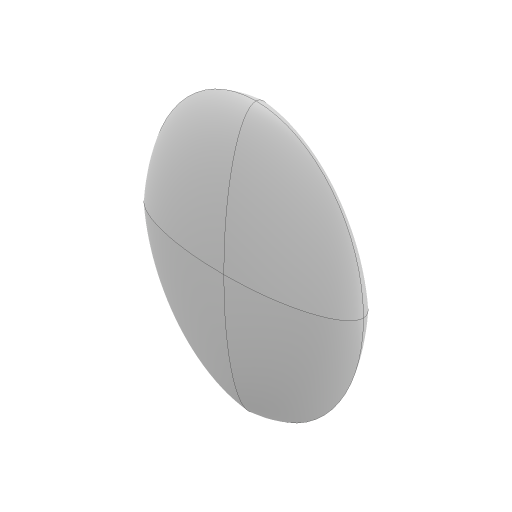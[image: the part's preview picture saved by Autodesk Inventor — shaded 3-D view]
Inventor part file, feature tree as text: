
AUTODESK INVENTOR PART (.ipt)
format: ipt  version: 2023 (Build 270158000, 158)  size: 343,552 bytes
history: native  units: in
note: dims shown in document units (in); Inventor stores cm internally (conversion verified against a paired STEP export)
features: mirror x3, sketch x3, loft x1
ambient origin geometry x8: Origin, YZ Plane, XZ Plane, XY Plane, X Axis, Y Axis, Z Axis, Center Point
bodies: Body1 (feature_tree)
feature tree (7):
  loft  "Loft1"
  mirror  "Mirror1"
  mirror  "Mirror2"
  mirror  "Mirror3"
  sketch  "Sketch1"  dims[d0=49.2126in d1=39.3701in]
  sketch  "Sketch7"  dims[d9=11.811in]
  sketch  "Sketch8"  dims[d10=39.3701in d11=11.811in d12=49.2126in d13=0.0in d14=90.0deg d15=0.0in d16=90.0deg d17=0.0in d18=90.0deg]
